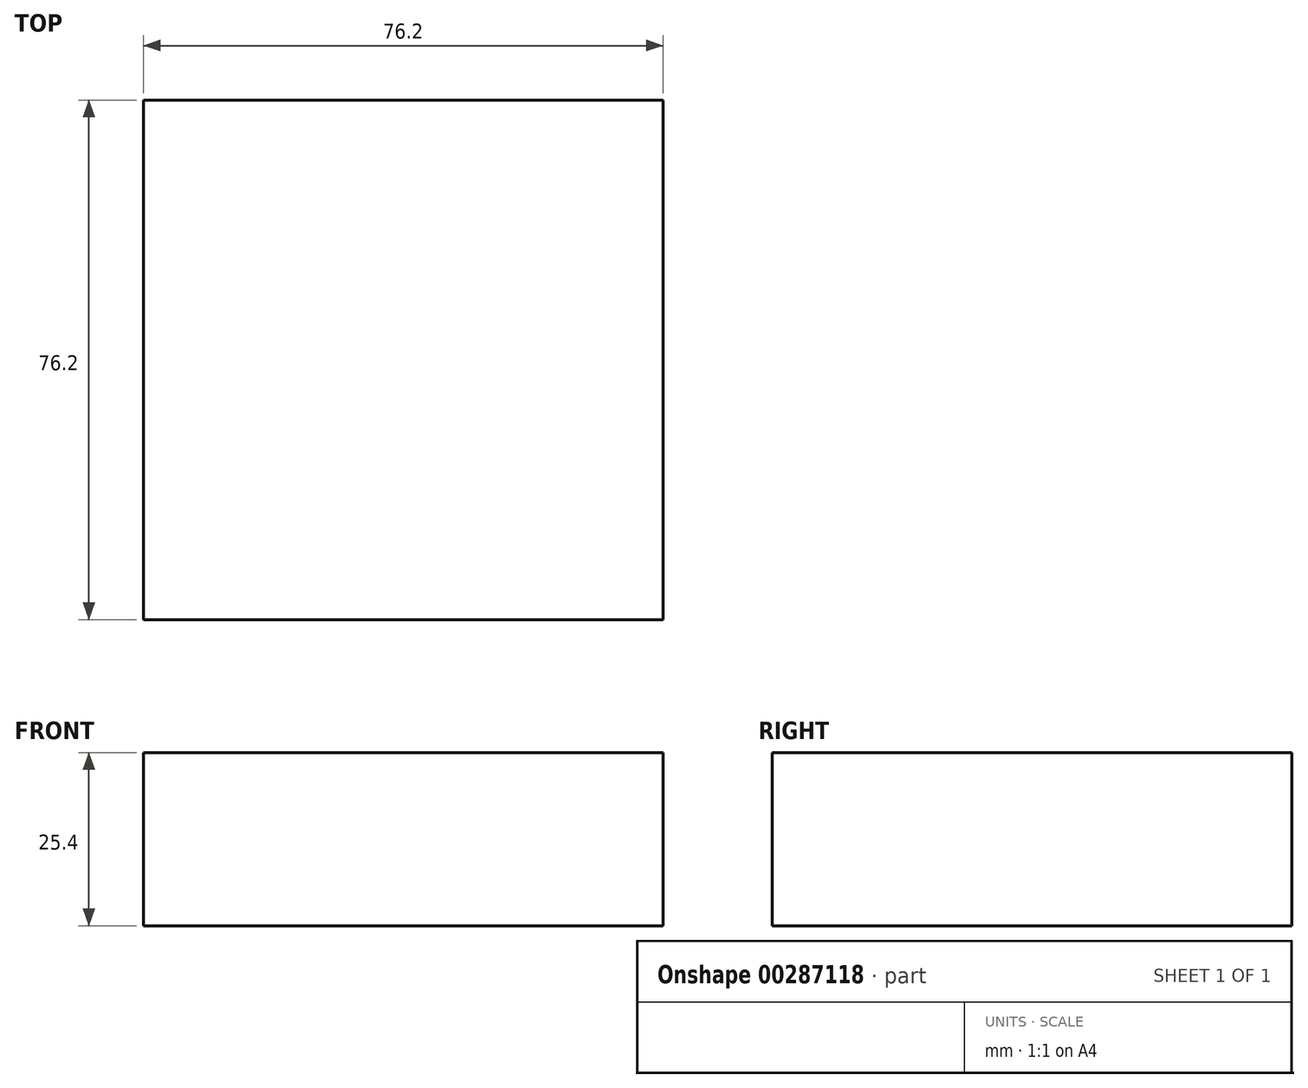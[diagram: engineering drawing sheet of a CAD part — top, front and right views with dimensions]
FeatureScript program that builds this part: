
annotation { "Feature Type Name" : "Feature", "Feature Type Description" : "" }
export const myFeature = defineFeature(function(context is Context, id is Id, definition is map)
    precondition{}
    {
        {
            var Q0;
            Q0=qCreatedBy(makeId("Top.planeOp"),FACE);
            var sketch = newSketch(context, id + "F0", { "sketchPlane" : qUnion([Q0])});
            skLineSegment(sketch, "E0.bottom", {"start": v(0, 0) * mm, "end": v(-76.2, 0) * mm});
            skLineSegment(sketch, "E0.top", {"start": v(0, -76.2) * mm, "end": v(-76.2, -76.2) * mm});
            skLineSegment(sketch, "E0.left", {"start": v(0, 0) * mm, "end": v(0, -76.2) * mm});
            skLineSegment(sketch, "E0.right", {"start": v(-76.2, 0) * mm, "end": v(-76.2, -76.2) * mm});
            skSolve(sketch);
        }
        {
            var Q0;
            Q0 = qSketchRegion(id + "F0", true);
            extrude(context, id + "F1", {"entities" : qUnion([Q0]), "depth" : 25.4 * mm});
        }
    });
